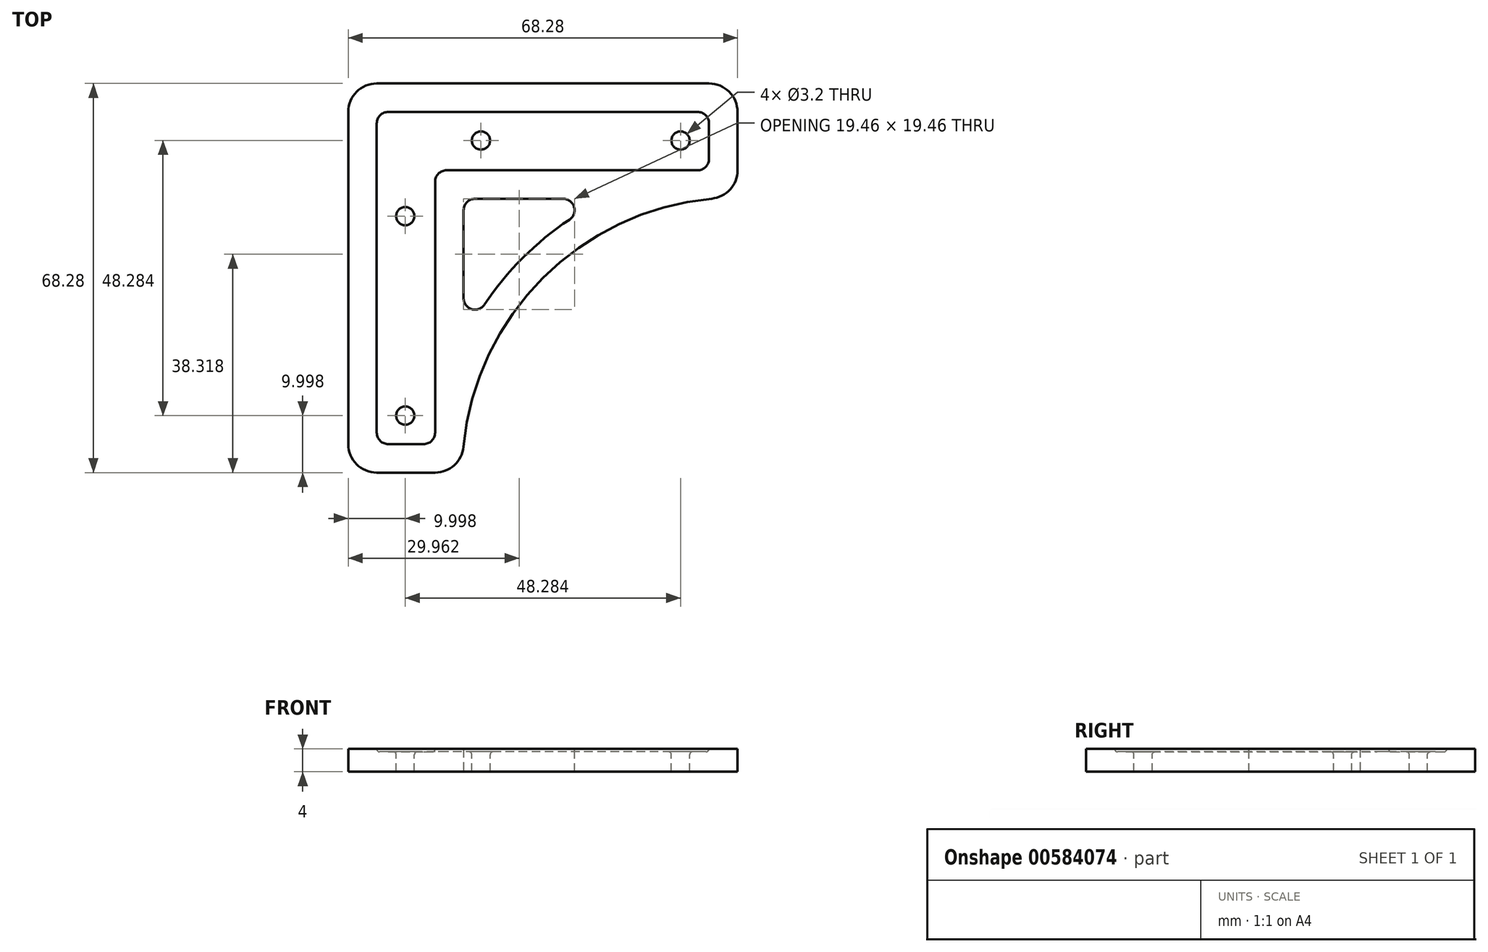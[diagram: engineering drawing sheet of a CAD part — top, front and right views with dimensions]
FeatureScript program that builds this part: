
annotation { "Feature Type Name" : "Feature", "Feature Type Description" : "" }
export const myFeature = defineFeature(function(context is Context, id is Id, definition is map)
    precondition{}
    {
        {
            var Q0;
            Q0=qCreatedBy(makeId("Top.planeOp"),FACE);
            var sketch = newSketch(context, id + "F0", { "sketchPlane" : qUnion([Q0])});
            skLineSegment(sketch, "E0", {"start": v(34.14, 34.14) * mm, "end": v(-34.14, 34.14) * mm});
            skLineSegment(sketch, "E1", {"start": v(-34.14, 34.14) * mm, "end": v(-34.14, -34.14) * mm});
            skLineSegment(sketch, "E2", {"start": v(-34.14, -34.14) * mm, "end": v(-14.14, -34.14) * mm});
            skLineSegment(sketch, "E3", {"start": v(34.14, 34.14) * mm, "end": v(34.14, 14.14) * mm});
            skArc(sketch, "E4", {"start": v(34.14, 14.14) * mm, "mid": v(0, 0) * mm, "end": v(-14.14, -34.14) * mm});
            skLineSegment(sketch, "E5", {"start": v(0, 34.14) * mm, "end": v(0, 0) * mm, "construction": true});
            skLineSegment(sketch, "E6", {"start": v(-34.14, 0) * mm, "end": v(0, 0) * mm, "construction": true});
            skSolve(sketch);
        }
        {
            var Q0;
            Q0=makeQuery(id+"F0.imprint","IMPRINT",FACE,{"disambiguationData":[TD([[makeQuery(id+"F0.imprint","IMPRINT",EDGE,{"derivedFrom":sQuery(id+"F0.wireOp",EDGE,"E0")}),1.0]])]});
            extrude(context, id + "F1", {"entities" : qUnion([Q0]), "depth" : 4 * mm, "offsetDistance" : 25 * mm});
        }
        {
            var Q0;
            Q0=makeQuery(id+"F1.opExtrude","CAP_FACE",FACE,{"disambiguationData":[OSD([sQuery(id+"F0.wireOp",EDGE,"E0"),sQuery(id+"F0.wireOp",EDGE,"E1"),sQuery(id+"F0.wireOp",EDGE,"E2"),sQuery(id+"F0.wireOp",EDGE,"E3"),sQuery(id+"F0.wireOp",EDGE,"E4")])],"isStart":false});
            var sketch = newSketch(context, id + "F2", { "sketchPlane" : qUnion([Q0])});
            skCircle(sketch, "E7", {"center": v(-24.14, -24.14) * mm, "radius": 1.6 * mm});
            skCircle(sketch, "E8", {"center": v(-24.14, 10.86) * mm, "radius": 1.6 * mm});
            skCircle(sketch, "E9", {"center": v(-10.86, 24.14) * mm, "radius": 1.6 * mm});
            skCircle(sketch, "E10", {"center": v(24.14, 24.14) * mm, "radius": 1.6 * mm});
            skLineSegment(sketch, "E11", {"start": v(-24.14, -34.14) * mm, "end": v(-24.14, -24.14) * mm, "construction": true});
            skLineSegment(sketch, "E12", {"start": v(34.14, 24.14) * mm, "end": v(24.14, 24.14) * mm, "construction": true});
            skSolve(sketch);
        }
        {
            var Q0;
            Q0=makeQuery(id+"F2.imprint","IMPRINT",FACE,{"disambiguationData":[TD([[makeQuery(id+"F2.imprint","IMPRINT",EDGE,{"derivedFrom":sQuery(id+"F2.wireOp",EDGE,"E7")}),1.0]])]});
            var Q1;
            Q1=makeQuery(id+"F2.imprint","IMPRINT",FACE,{"disambiguationData":[TD([[makeQuery(id+"F2.imprint","IMPRINT",EDGE,{"derivedFrom":sQuery(id+"F2.wireOp",EDGE,"E9")}),1.0]])]});
            var Q2;
            Q2=makeQuery(id+"F2.imprint","IMPRINT",FACE,{"disambiguationData":[TD([[makeQuery(id+"F2.imprint","IMPRINT",EDGE,{"derivedFrom":sQuery(id+"F2.wireOp",EDGE,"E10")}),1.0]])]});
            var Q3;
            Q3=makeQuery(id+"F2.imprint","IMPRINT",FACE,{"disambiguationData":[TD([[makeQuery(id+"F2.imprint","IMPRINT",EDGE,{"derivedFrom":sQuery(id+"F2.wireOp",EDGE,"E8")}),1.0]])]});
            extrude(context, id + "F3", {"entities" : qUnion([Q0, Q1, Q2, Q3]), "operationType" : NewBodyOperationType.REMOVE, "endBound" : BoundingType.THROUGH_ALL, "oppositeDirection" : true, "depth" : 25 * mm, "offsetDistance" : 25 * mm});
        }
        {
            var Q0;
            Q0=makeQuery(id+"F1.opExtrude","SWEPT_EDGE",EDGE,{"disambiguationData":[OSD([sQuery(id+"F0.wireOp",EDGE,"E2"),sQuery(id+"F0.wireOp",EDGE,"E4")])]});
            var Q1;
            Q1=makeQuery(id+"F1.opExtrude","SWEPT_EDGE",EDGE,{"disambiguationData":[OSD([sQuery(id+"F0.wireOp",EDGE,"E1"),sQuery(id+"F0.wireOp",EDGE,"E2")])]});
            var Q2;
            Q2=makeQuery(id+"F1.opExtrude","SWEPT_EDGE",EDGE,{"disambiguationData":[OSD([sQuery(id+"F0.wireOp",EDGE,"E3"),sQuery(id+"F0.wireOp",EDGE,"E4")])]});
            var Q3;
            Q3=makeQuery(id+"F1.opExtrude","SWEPT_EDGE",EDGE,{"disambiguationData":[OSD([sQuery(id+"F0.wireOp",EDGE,"E0"),sQuery(id+"F0.wireOp",EDGE,"E3")])]});
            var Q4;
            Q4=makeQuery(id+"F1.opExtrude","SWEPT_EDGE",EDGE,{"disambiguationData":[OSD([sQuery(id+"F0.wireOp",EDGE,"E0"),sQuery(id+"F0.wireOp",EDGE,"E1")])]});
            fillet(context, id + "F4", {"entities" : qUnion([Q0, Q1, Q2, Q3, Q4]), "radius" : 5 * mm, "tangentPropagation" : true, "allowEdgeOverflow" : false});
        }
        {
            var Q0;
            Q0=makeQuery(id+"F1.opExtrude","CAP_FACE",FACE,{"disambiguationData":[OSD([sQuery(id+"F0.wireOp",EDGE,"E0"),sQuery(id+"F0.wireOp",EDGE,"E1"),sQuery(id+"F0.wireOp",EDGE,"E2"),sQuery(id+"F0.wireOp",EDGE,"E3"),sQuery(id+"F0.wireOp",EDGE,"E4")])],"isStart":false});
            var sketch = newSketch(context, id + "F5", { "sketchPlane" : qUnion([Q0])});
            skLineSegment(sketch, "E13", {"start": v(27.14, 29.14) * mm, "end": v(-27.14, 29.14) * mm});
            skLineSegment(sketch, "E14", {"start": v(-29.14, 27.14) * mm, "end": v(-29.14, -27.14) * mm});
            skLineSegment(sketch, "E15", {"start": v(-27.14, -29.14) * mm, "end": v(-20.9, -29.14) * mm});
            skLineSegment(sketch, "E16", {"start": v(-18.9, -27.14) * mm, "end": v(-18.9, 16.9) * mm});
            skLineSegment(sketch, "E17", {"start": v(29.14, 27.14) * mm, "end": v(29.14, 20.9) * mm});
            skLineSegment(sketch, "E18", {"start": v(27.14, 18.9) * mm, "end": v(-16.9, 18.9) * mm});
            skPoint(sketch, "E19.visualSharp", {"position": v(-29.14, 29.14) * mm});
            skArc(sketch, "E19.filletArc", {"start": v(-27.14, 29.14) * mm, "mid": v(-28.56, 28.56) * mm, "end": v(-29.14, 27.14) * mm});
            skPoint(sketch, "E20.visualSharp", {"position": v(-18.9, 18.9) * mm});
            skArc(sketch, "E20.filletArc", {"start": v(-16.9, 18.9) * mm, "mid": v(-18.32, 18.32) * mm, "end": v(-18.9, 16.9) * mm});
            skPoint(sketch, "E21.visualSharp", {"position": v(29.14, 18.9) * mm});
            skArc(sketch, "E21.filletArc", {"start": v(27.14, 18.9) * mm, "mid": v(28.56, 19.5) * mm, "end": v(29.14, 20.9) * mm});
            skPoint(sketch, "E22.visualSharp", {"position": v(29.14, 29.14) * mm});
            skArc(sketch, "E22.filletArc", {"start": v(29.14, 27.14) * mm, "mid": v(28.56, 28.56) * mm, "end": v(27.14, 29.14) * mm});
            skPoint(sketch, "E23.visualSharp", {"position": v(-18.9, -29.14) * mm});
            skArc(sketch, "E23.filletArc", {"start": v(-20.9, -29.14) * mm, "mid": v(-19.5, -28.56) * mm, "end": v(-18.9, -27.14) * mm});
            skPoint(sketch, "E24.visualSharp", {"position": v(-29.14, -29.14) * mm});
            skArc(sketch, "E24.filletArc", {"start": v(-29.14, -27.14) * mm, "mid": v(-28.56, -28.56) * mm, "end": v(-27.14, -29.14) * mm});
            skSolve(sketch);
        }
        {
            var Q0;
            Q0=makeQuery(id+"F5.imprint","IMPRINT",FACE,{"disambiguationData":[TD([[makeQuery(id+"F5.imprint","IMPRINT",EDGE,{"derivedFrom":sQuery(id+"F5.wireOp",EDGE,"E13")}),1.0]])]});
            extrude(context, id + "F6", {"entities" : qUnion([Q0]), "operationType" : NewBodyOperationType.REMOVE, "oppositeDirection" : true, "depth" : 0.5 * mm, "offsetDistance" : 25 * mm});
        }
        {
            var Q0;
            Q0=makeQuery(id+"F6.boolean.opBoolean","COPY",FACE,{"derivedFrom":makeQuery(id+"F6.opExtrude","CAP_FACE",FACE,{"disambiguationData":[OSD([sQuery(id+"F2.wireOp",EDGE,"E7"),sQuery(id+"F2.wireOp",EDGE,"E8"),sQuery(id+"F2.wireOp",EDGE,"E9"),sQuery(id+"F2.wireOp",EDGE,"E10"),sQuery(id+"F5.wireOp",EDGE,"62291f06-3296-4faf-adc0-8874e116e12e.0"),sQuery(id+"F5.wireOp",EDGE,"62291f06-3296-4faf-adc0-8874e116e12e.1"),sQuery(id+"F5.wireOp",EDGE,"62291f06-3296-4faf-adc0-8874e116e12e.2"),sQuery(id+"F5.wireOp",EDGE,"62291f06-3296-4faf-adc0-8874e116e12e.3"),sQuery(id+"F5.wireOp",EDGE,"62291f06-3296-4faf-adc0-8874e116e12e.4"),sQuery(id+"F5.wireOp",EDGE,"62291f06-3296-4faf-adc0-8874e116e12e.5"),sQuery(id+"F5.wireOp",EDGE,"62291f06-3296-4faf-adc0-8874e116e12e.6"),sQuery(id+"F5.wireOp",EDGE,"62291f06-3296-4faf-adc0-8874e116e12e.7"),sQuery(id+"F5.wireOp",EDGE,"62291f06-3296-4faf-adc0-8874e116e12e.8"),sQuery(id+"F5.wireOp",EDGE,"62291f06-3296-4faf-adc0-8874e116e12e.9")])],"isStart":false})});
            fillet(context, id + "F7", {"entities" : qUnion([Q0]), "radius" : 0.5 * mm, "tangentPropagation" : true, "allowEdgeOverflow" : false});
        }
        {
            var Q0;
            Q0=makeQuery(id+"F1.opExtrude","CAP_FACE",FACE,{"disambiguationData":[OSD([sQuery(id+"F0.wireOp",EDGE,"E0"),sQuery(id+"F0.wireOp",EDGE,"E1"),sQuery(id+"F0.wireOp",EDGE,"E2"),sQuery(id+"F0.wireOp",EDGE,"E3"),sQuery(id+"F0.wireOp",EDGE,"E4")])],"isStart":false});
            var sketch = newSketch(context, id + "F8", { "sketchPlane" : qUnion([Q0])});
            skArc(sketch, "E25.0", {"start": v(11.1, 13.9) * mm, "mid": v(-3.54, 3.54) * mm, "end": v(-13.9, -11.1) * mm});
            skLineSegment(sketch, "E26", {"start": v(-13.9, -11.1) * mm, "end": v(-13.9, 13.9) * mm});
            skLineSegment(sketch, "E27", {"start": v(-13.9, 13.9) * mm, "end": v(11.1, 13.9) * mm});
            skSolve(sketch);
        }
        {
            var Q0;
            Q0=makeQuery(id+"F8.imprint","IMPRINT",FACE,{"disambiguationData":[TD([[makeQuery(id+"F8.imprint","IMPRINT",EDGE,{"derivedFrom":sQuery(id+"F8.wireOp",EDGE,"E25.0")}),-1.0]])]});
            extrude(context, id + "F9", {"entities" : qUnion([Q0]), "operationType" : NewBodyOperationType.REMOVE, "endBound" : BoundingType.THROUGH_ALL, "oppositeDirection" : true, "depth" : 25 * mm, "offsetDistance" : 25 * mm});
        }
        {
            var Q0;
            Q0=makeQuery(id+"F9.boolean.opBoolean","COPY",EDGE,{"derivedFrom":makeQuery(id+"F9.opExtrude","SWEPT_EDGE",EDGE,{"disambiguationData":[OSD([sQuery(id+"F8.wireOp",EDGE,"E26"),sQuery(id+"F8.wireOp",EDGE,"E27")])]})});
            var Q1;
            Q1=makeQuery(id+"F9.boolean.opBoolean","COPY",EDGE,{"derivedFrom":makeQuery(id+"F9.opExtrude","SWEPT_EDGE",EDGE,{"disambiguationData":[OSD([sQuery(id+"F8.wireOp",EDGE,"E25.0"),sQuery(id+"F8.wireOp",EDGE,"E26")])]})});
            var Q2;
            Q2=makeQuery(id+"F9.boolean.opBoolean","COPY",EDGE,{"derivedFrom":makeQuery(id+"F9.opExtrude","SWEPT_EDGE",EDGE,{"disambiguationData":[OSD([sQuery(id+"F8.wireOp",EDGE,"E25.0"),sQuery(id+"F8.wireOp",EDGE,"E27")])]})});
            fillet(context, id + "F10", {"entities" : qUnion([Q0, Q1, Q2]), "radius" : 2 * mm, "tangentPropagation" : true, "allowEdgeOverflow" : false});
        }
    });
